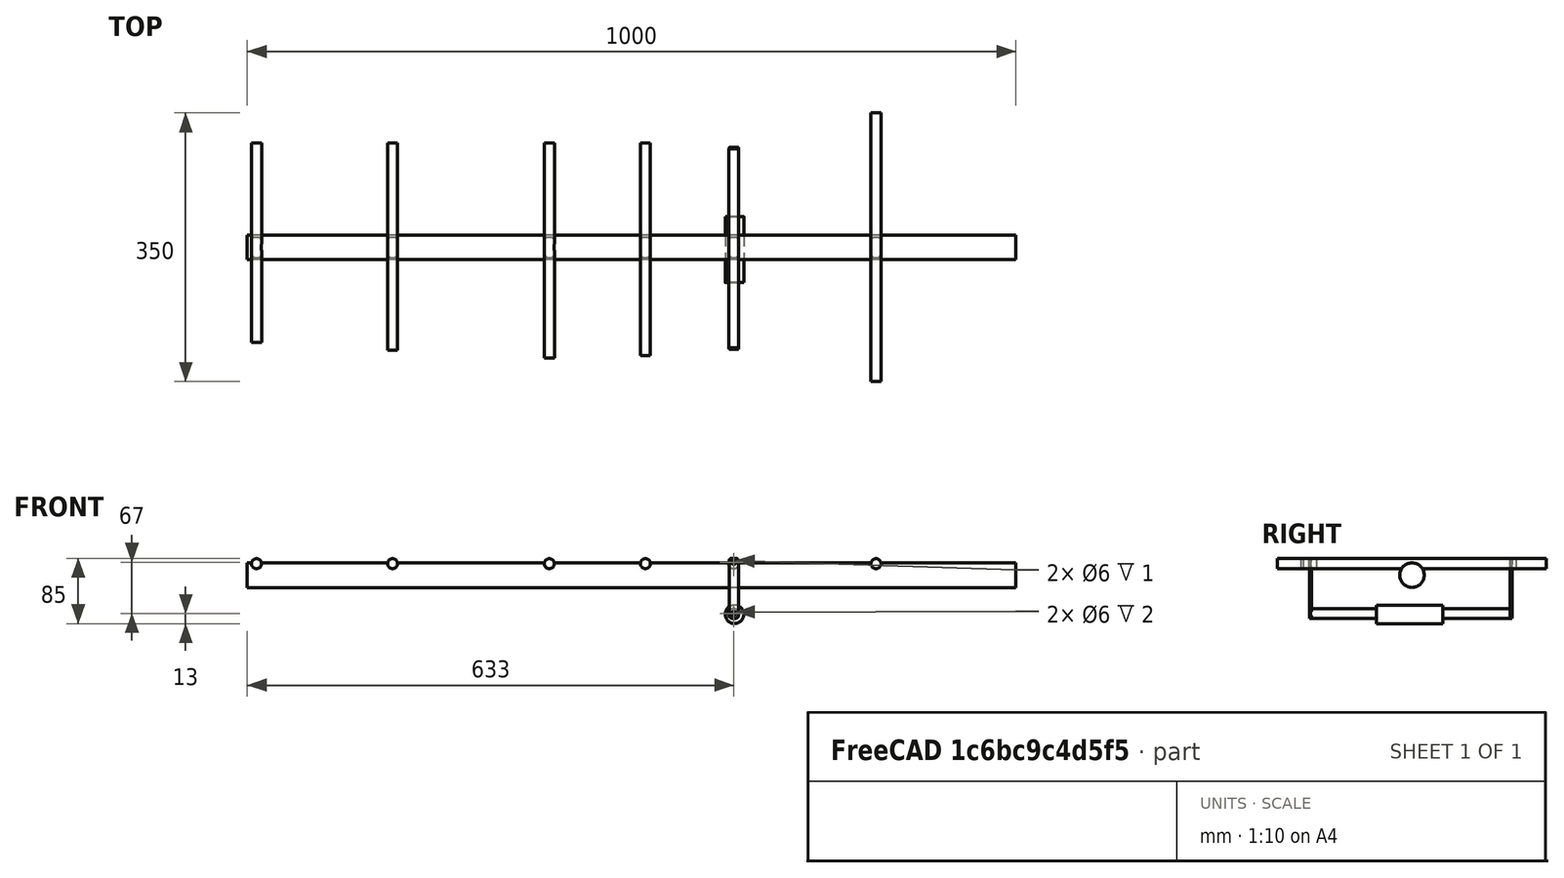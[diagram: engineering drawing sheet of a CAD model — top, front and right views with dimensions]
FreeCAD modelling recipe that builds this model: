
FCSTD DOCUMENT  (FreeCAD 0.18R4 (GitTag))
Label: Antena
License: All rights reserved
LicenseURL: http://en.wikipedia.org/wiki/All_rights_reserved
objects: Part::Cylinder×13, Part::Box×2, Part::Fuse×2, Part::Cut×2, Part::Fillet×2, Part::MultiFuse×1
note: 22 computed .brp shape members not serialized (recipe doc carries the construction recipe); baked Part::Feature solids carry a one-line shape summary decoded from their .brp

FEATURE [Part::Cylinder] Cylinder  label="Base"
  Angle = 360
  AttacherType = Attacher::AttachEngine3D
  Height = 1000
  Placement = pos=(0,0,-166) rot=(0,0,1;0rad)
  Radius = 16
FEATURE [Part::Cylinder] Cylinder001  label="Reflector"
  Angle = 360
  AttacherType = Attacher::AttachEngine3D
  Height = 350
  Placement = pos=(15,175,16) rot=(0,0.707107,-0.707107;3.14159rad)
  Radius = 6.5
FEATURE [Part::Cylinder] Cylinder002  label="Director1"
  Angle = 360
  AttacherType = Attacher::AttachEngine3D
  Height = 277
  Placement = pos=(15,136,316) rot=(0,0.707107,-0.707107;3.14159rad)
  Radius = 6.5
FEATURE [Part::Cylinder] Cylinder003  label="DipoloSup"
  Angle = 360
  AttacherType = Attacher::AttachEngine3D
  Height = 260
  Placement = pos=(15,128,201) rot=(0,0.707107,-0.707107;3.14159rad)
  Radius = 6.5
FEATURE [Part::Cylinder] Cylinder004  label="DipoloInf"
  Angle = 360
  AttacherType = Attacher::AttachEngine3D
  Height = 260
  Placement = pos=(-50,128,201) rot=(0,0.707107,-0.707107;3.14159rad)
  Radius = 6.5
FEATURE [Part::Box] Box  label="union1"
  AttacherType = Attacher::AttachEngine3D
  Height = 12
  Length = 78
  Placement = pos=(-56,129,195) rot=(0,0,1;0rad)
  Width = 2
FEATURE [Part::Cylinder] Cylinder005  label="Cilindro"
  Angle = 360
  AttacherType = Attacher::AttachEngine3D
  Height = 4
  Placement = pos=(-50,132,201) rot=(1,0,0;1.5708rad)
  Radius = 3
FEATURE [Part::Cylinder] Cylinder006  label="Cilindro001"
  Angle = 360
  AttacherType = Attacher::AttachEngine3D
  Height = 4
  Placement = pos=(17,132,201) rot=(1,0,0;1.5708rad)
  Radius = 3
FEATURE [Part::Fuse] Fusion
  Base = -> Cylinder005
  Tool = -> Cylinder006
FEATURE [Part::Cut] Cut
  Base = -> Box
  Tool = -> Fusion
FEATURE [Part::Fillet] Fillet  label="Union"
  Base = -> Cut
  Edges = 4 edges r=3.2: [Edge2,Edge4,Edge11,Edge16]
  Placement = pos=(0,-1,0) rot=(0,0,1;0rad)
FEATURE [Part::Cylinder] Cylinder007  label="Cilindro002"
  Angle = 360
  AttacherType = Attacher::AttachEngine3D
  Height = 4
  Placement = pos=(-50,132,201) rot=(1,0,0;1.5708rad)
  Radius = 3
FEATURE [Part::Box] Box001  label="union002"
  AttacherType = Attacher::AttachEngine3D
  Height = 12
  Length = 78
  Placement = pos=(-56,129,195) rot=(0,0,1;0rad)
  Width = 2
FEATURE [Part::Cylinder] Cylinder008  label="Cilindro003"
  Angle = 360
  AttacherType = Attacher::AttachEngine3D
  Height = 4
  Placement = pos=(17,132,201) rot=(1,0,0;1.5708rad)
  Radius = 3
FEATURE [Part::Fuse] Fusion001
  Base = -> Cylinder007
  Tool = -> Cylinder008
FEATURE [Part::Cut] Cut001
  Base = -> Box001
  Tool = -> Fusion001
FEATURE [Part::Fillet] Fillet001  label="Union001"
  Base = -> Cut001
  Edges = 4 edges r=3.2: [Edge2,Edge4,Edge11,Edge16]
  Placement = pos=(0,-262,0) rot=(0,0,1;0rad)
FEATURE [Part::Cylinder] Cylinder009  label="Cilindro004"
  Angle = 360
  AttacherType = Attacher::AttachEngine3D
  Height = 86
  Placement = pos=(-51,40,200) rot=(1,0,0;1.5708rad)
  Radius = 12
FEATURE [Part::Cylinder] Cylinder010  label="Director002"
  Angle = 360
  AttacherType = Attacher::AttachEngine3D
  Height = 280
  Placement = pos=(15,136,441) rot=(0,0.707107,-0.707107;3.14159rad)
  Radius = 6.5
FEATURE [Part::Cylinder] Cylinder011  label="Director003"
  Angle = 360
  AttacherType = Attacher::AttachEngine3D
  Height = 270
  Placement = pos=(15,136,645) rot=(0,0.707107,-0.707107;3.14159rad)
  Radius = 6.5
FEATURE [Part::Cylinder] Cylinder012  label="Director004"
  Angle = 360
  AttacherType = Attacher::AttachEngine3D
  Height = 260
  Placement = pos=(15,136,822) rot=(0,0.707107,-0.707107;3.14159rad)
  Radius = 6.5
FEATURE [Part::MultiFuse] Fusion002  label="Antena completa"
  Placement = pos=(-166,0,0) rot=(0,-1,0;1.5708rad)
  Shapes = -> [Cylinder,Cylinder001,Cylinder002,Cylinder003,Cylinder004,Fillet,Fillet001,Cylinder009,Cylinder010,Cylinder011,Cylinder012]
